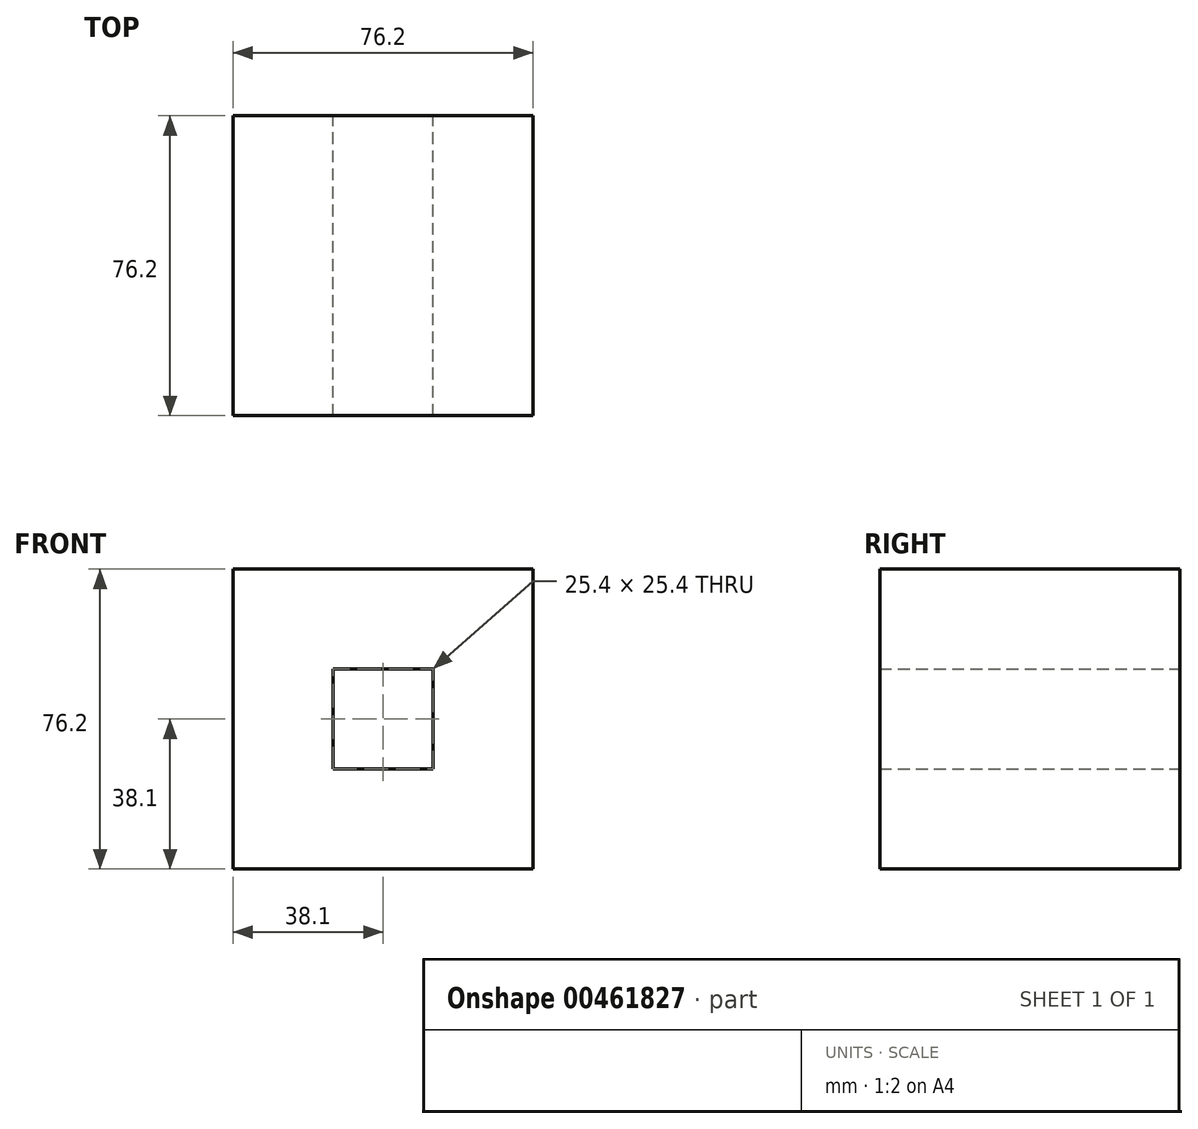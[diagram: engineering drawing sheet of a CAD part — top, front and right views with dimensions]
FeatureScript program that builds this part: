
annotation { "Feature Type Name" : "Feature", "Feature Type Description" : "" }
export const myFeature = defineFeature(function(context is Context, id is Id, definition is map)
    precondition{}
    {
        {
            var Q0;
            Q0=qCreatedBy(makeId("Front.planeOp"),FACE);
            var sketch = newSketch(context, id + "F0", { "sketchPlane" : qUnion([Q0])});
            skLineSegment(sketch, "E0.bottom", {"start": v(38.1, -38.1) * mm, "end": v(-38.1, -38.1) * mm});
            skLineSegment(sketch, "E0.top", {"start": v(38.1, 38.1) * mm, "end": v(-38.1, 38.1) * mm});
            skLineSegment(sketch, "E0.left", {"start": v(38.1, -38.1) * mm, "end": v(38.1, 38.1) * mm});
            skLineSegment(sketch, "E0.right", {"start": v(-38.1, -38.1) * mm, "end": v(-38.1, 38.1) * mm});
            skPoint(sketch, "E0.middle", {"position": v(0, 0) * mm});
            skSolve(sketch);
        }
        {
            var Q0;
            Q0=qCreatedBy(makeId("Front.planeOp"),FACE);
            var sketch = newSketch(context, id + "F1", { "sketchPlane" : qUnion([Q0])});
            skLineSegment(sketch, "E1.bottom", {"start": v(-12.7, -12.7) * mm, "end": v(12.7, -12.7) * mm});
            skLineSegment(sketch, "E1.top", {"start": v(-12.7, 12.7) * mm, "end": v(12.7, 12.7) * mm});
            skLineSegment(sketch, "E1.left", {"start": v(-12.7, -12.7) * mm, "end": v(-12.7, 12.7) * mm});
            skLineSegment(sketch, "E1.right", {"start": v(12.7, -12.7) * mm, "end": v(12.7, 12.7) * mm});
            skPoint(sketch, "E1.middle", {"position": v(0, 0) * mm});
            skSolve(sketch);
        }
        {
            var Q0;
            Q0=makeQuery(id+"F0.imprint","IMPRINT",FACE,{"disambiguationData":[TD([[makeQuery(id+"F0.imprint","IMPRINT",EDGE,{"derivedFrom":sQuery(id+"F0.wireOp",EDGE,"E0.bottom")}),-1.0]])]});
            extrude(context, id + "F2", {"entities" : qUnion([Q0]), "depth" : 76.2 * mm});
        }
        {
            var Q0;
            Q0=makeQuery(id+"F1.imprint","IMPRINT",FACE,{"disambiguationData":[TD([[makeQuery(id+"F1.imprint","IMPRINT",EDGE,{"derivedFrom":sQuery(id+"F1.wireOp",EDGE,"E1.bottom")}),1.0]])]});
            extrude(context, id + "F3", {"entities" : qUnion([Q0]), "operationType" : NewBodyOperationType.REMOVE, "endBound" : BoundingType.THROUGH_ALL, "depth" : 76.2 * mm});
        }
    });
